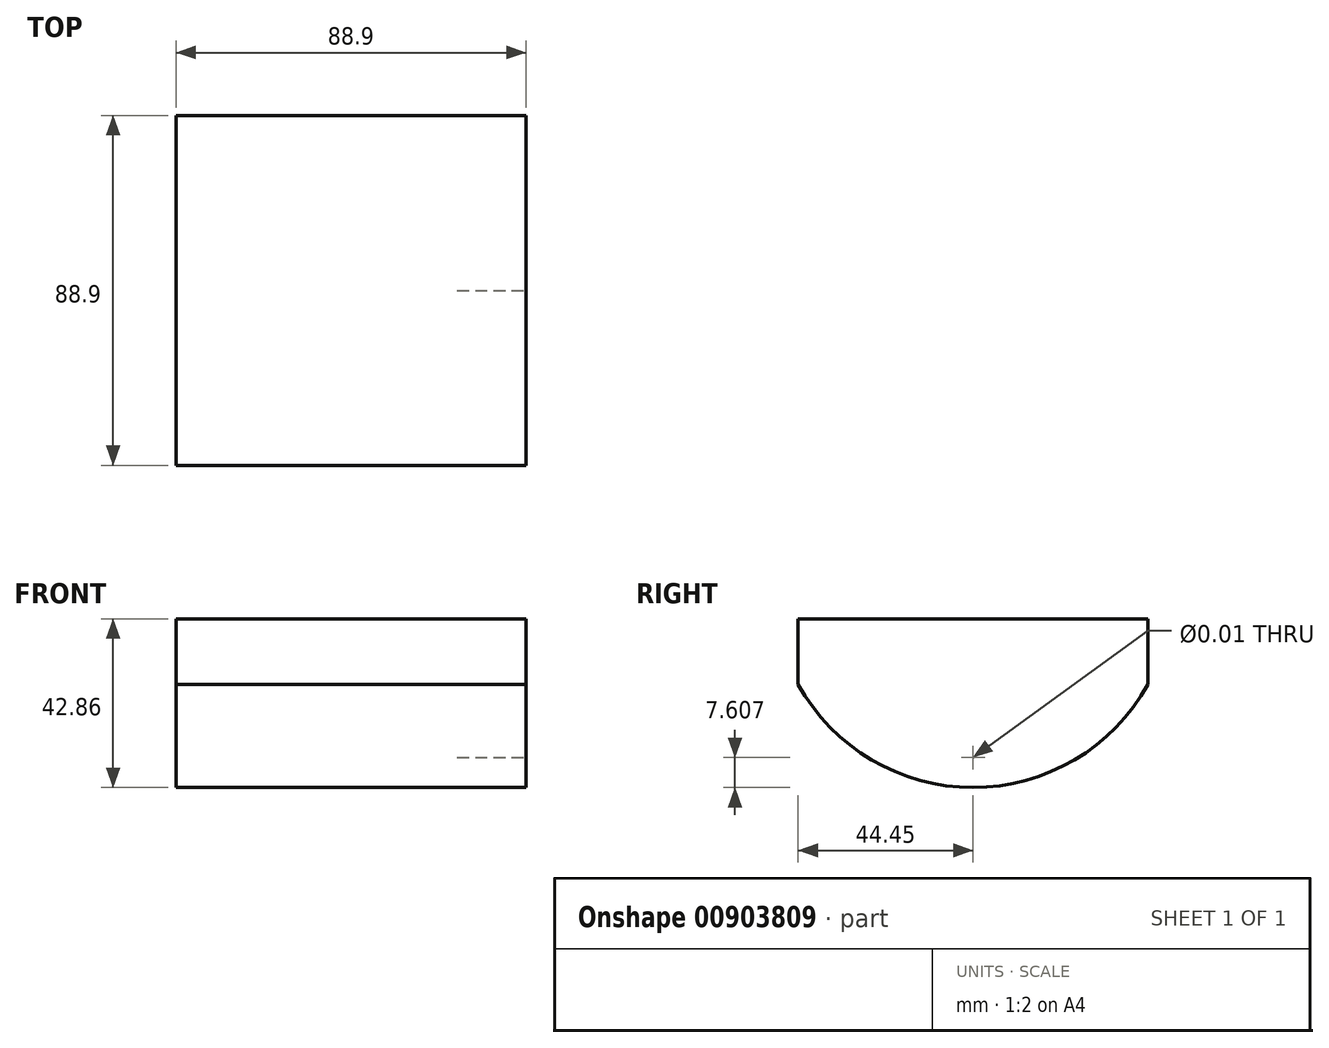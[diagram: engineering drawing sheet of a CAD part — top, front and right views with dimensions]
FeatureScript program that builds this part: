
annotation { "Feature Type Name" : "Feature", "Feature Type Description" : "" }
export const myFeature = defineFeature(function(context is Context, id is Id, definition is map)
    precondition{}
    {
        {
            var Q0;
            Q0=qCreatedBy(makeId("Right.planeOp"),FACE);
            var sketch = newSketch(context, id + "F0", { "sketchPlane" : qUnion([Q0])});
            skArc(sketch, "E0", {"start": v(-44.45, 26.2) * mm, "mid": v(0, 0) * mm, "end": v(44.45, 26.2) * mm});
            skLineSegment(sketch, "E1", {"start": v(-44.45, 26.2) * mm, "end": v(-44.45, 42.86) * mm});
            skLineSegment(sketch, "E2", {"start": v(-44.45, 42.86) * mm, "end": v(44.45, 42.86) * mm});
            skLineSegment(sketch, "E3", {"start": v(44.45, 42.86) * mm, "end": v(44.45, 26.2) * mm});
            skSolve(sketch);
        }
        {
            var Q0;
            Q0 = qSketchRegion(id + "F0", true);
            extrude(context, id + "F1", {"entities" : qUnion([Q0]), "depth" : 44.45 * mm, "offsetDistance" : 25.4 * mm, "hasSecondDirection" : true, "secondDirectionOppositeDirection" : true, "secondDirectionDepth" : 44.45 * mm});
        }
        {
            var Q0;
            Q0=makeQuery(id+"F1.opExtrude","CAP_FACE",FACE,{"disambiguationData":[OSD([sQuery(id+"F0.wireOp",EDGE,"E0"),sQuery(id+"F0.wireOp",EDGE,"E1"),sQuery(id+"F0.wireOp",EDGE,"E2"),sQuery(id+"F0.wireOp",EDGE,"E3")])],"isStart":false});
            cPlane(context, id + "F2", {"entities" : qUnion([Q0]), "cplaneType" : CPlaneType.OFFSET, "offset" : 0 * mm, "width" : 152.4 * mm, "height" : 152.4 * mm});
        }
        {
            var Q0;
            Q0=qCreatedBy(id+"F2.planeOp",FACE);
            var sketch = newSketch(context, id + "F3", { "sketchPlane" : qUnion([Q0])});
            skPoint(sketch, "E4", {"position": v(0, 7.6) * mm});
            skSolve(sketch);
        }
        {
            var Q0;
            Q0=sQuery(id+"F3.wireOp",VERTEX,"E4");
            var Q1;
            Q1=makeQuery(id+"F1.opExtrude","SWEPT_BODY",BODY,{"disambiguationData":[OSD([sQuery(id+"F0.wireOp",EDGE,"E0"),sQuery(id+"F0.wireOp",EDGE,"E1"),sQuery(id+"F0.wireOp",EDGE,"E2"),sQuery(id+"F0.wireOp",EDGE,"E3")])]});
            hole(context, id + "F4", {"style" : HoleStyle.SIMPLE, "endStyle" : HoleEndStyle.BLIND, "standardTappedOrClearance" : lookupTablePath({ "standard" : "ANSI", "size" : "5/16 (0.31)", "type" : "Drilled" }), "standardBlindInLast" : lookupTablePath({ "standard" : "ANSI", "size" : "5/16", "type" : "Drilled" }), "holeDiameter" : 5 / 406.4 * mm, "majorDiameter" : 6.35 * mm, "holeDepth" : 17.46 * mm, "tappedDepth" : 12.06 * mm, "tapClearance" : 3, "locations" : qUnion([Q0]), "scope" : qUnion([Q1])});
        }
    });
